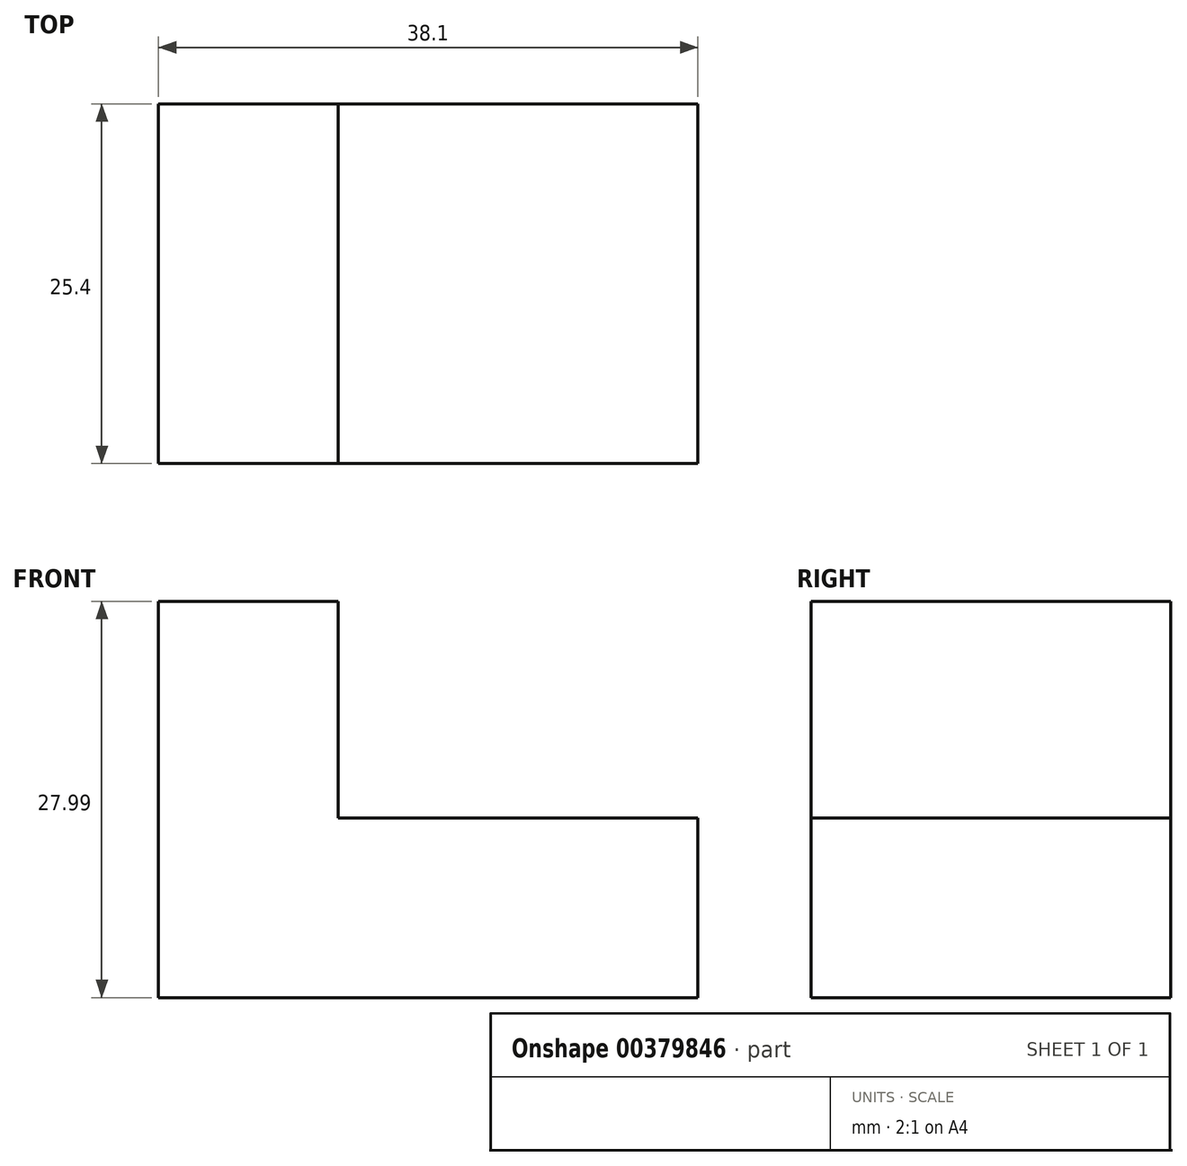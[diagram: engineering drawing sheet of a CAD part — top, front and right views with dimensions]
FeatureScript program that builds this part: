
annotation { "Feature Type Name" : "Feature", "Feature Type Description" : "" }
export const myFeature = defineFeature(function(context is Context, id is Id, definition is map)
    precondition{}
    {
        {
            var Q0;
            Q0=qCreatedBy(makeId("Front.planeOp"),FACE);
            var sketch = newSketch(context, id + "F0", { "sketchPlane" : qUnion([Q0])});
            skLineSegment(sketch, "E0", {"start": v(0, 0) * mm, "end": v(38.1, 0) * mm});
            skLineSegment(sketch, "E1", {"start": v(38.1, 0) * mm, "end": v(38.1, 12.7) * mm});
            skLineSegment(sketch, "E2", {"start": v(38.1, 12.7) * mm, "end": v(12.7, 12.7) * mm});
            skLineSegment(sketch, "E3", {"start": v(12.7, 12.7) * mm, "end": v(12.7, 27.99) * mm});
            skLineSegment(sketch, "E4", {"start": v(12.7, 27.99) * mm, "end": v(0, 27.99) * mm});
            skLineSegment(sketch, "E5", {"start": v(0, 27.99) * mm, "end": v(0, 0) * mm});
            skSolve(sketch);
        }
        {
            var Q0;
            Q0=makeQuery(id+"F0.imprint","IMPRINT",FACE,{"disambiguationData":[TD([[makeQuery(id+"F0.imprint","IMPRINT",EDGE,{"derivedFrom":sQuery(id+"F0.wireOp",EDGE,"E0")}),1.0]])]});
            extrude(context, id + "F1", {"entities" : qUnion([Q0]), "depth" : 25.4 * mm});
        }
    });
